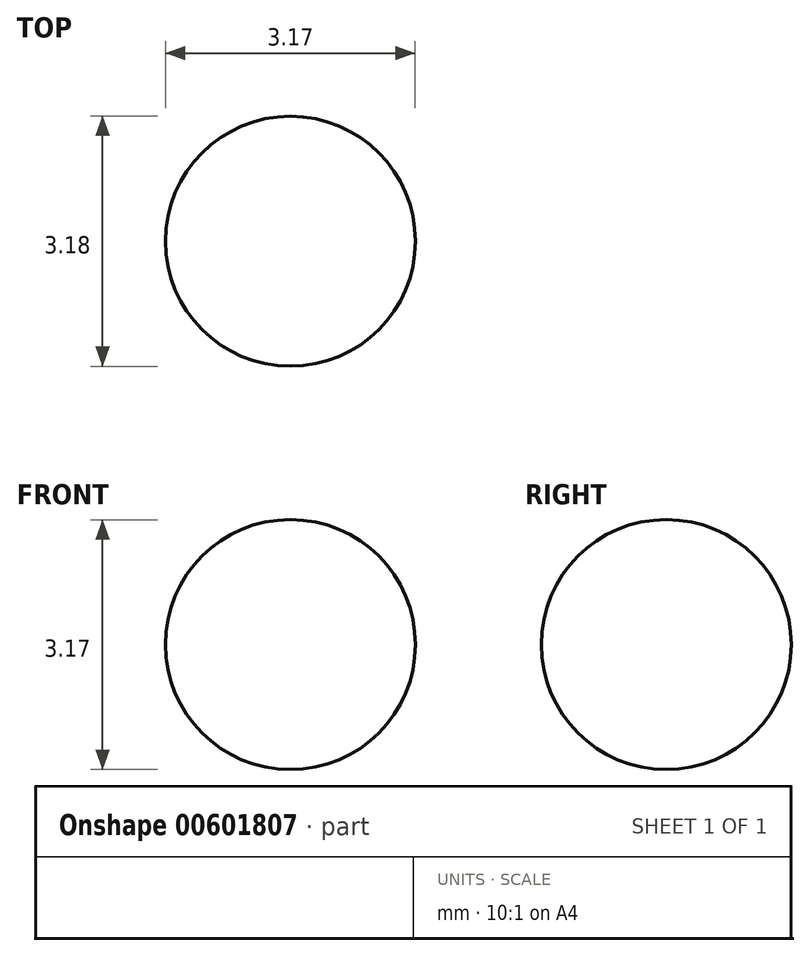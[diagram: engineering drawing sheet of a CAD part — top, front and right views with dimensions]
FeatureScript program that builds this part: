
annotation { "Feature Type Name" : "Feature", "Feature Type Description" : "" }
export const myFeature = defineFeature(function(context is Context, id is Id, definition is map)
    precondition{}
    {
        {
            var Q0;
            Q0=qCreatedBy(makeId("Front.planeOp"),FACE);
            var sketch = newSketch(context, id + "F0", { "sketchPlane" : qUnion([Q0])});
            skCircle(sketch, "E0", {"center": v(28.57, 27.89) * mm, "radius": 1.59 * mm});
            skLineSegment(sketch, "E1", {"start": v(28.57, 29.47) * mm, "end": v(28.57, 26.3) * mm});
            skSolve(sketch);
        }
        {
            var Q0;
            {var subQ0=sQuery(id+"F0.wireOp",EDGE,"E1");Q0=makeQuery(id+"F0.imprint","IMPRINT",FACE,{"disambiguationData":[TD([[makeQuery(id+"F0.imprint","IMPRINT",EDGE,{"derivedFrom":subQ0}),-1.0]])]});}
            var Q1;
            Q1=sQuery(id+"F0.wireOp",EDGE,"E1");
            revolve(context, id + "F1", {"entities" : qUnion([Q0]), "axis" : qUnion([Q1]), "revolveType" : RevolveType.FULL});
        }
    });
